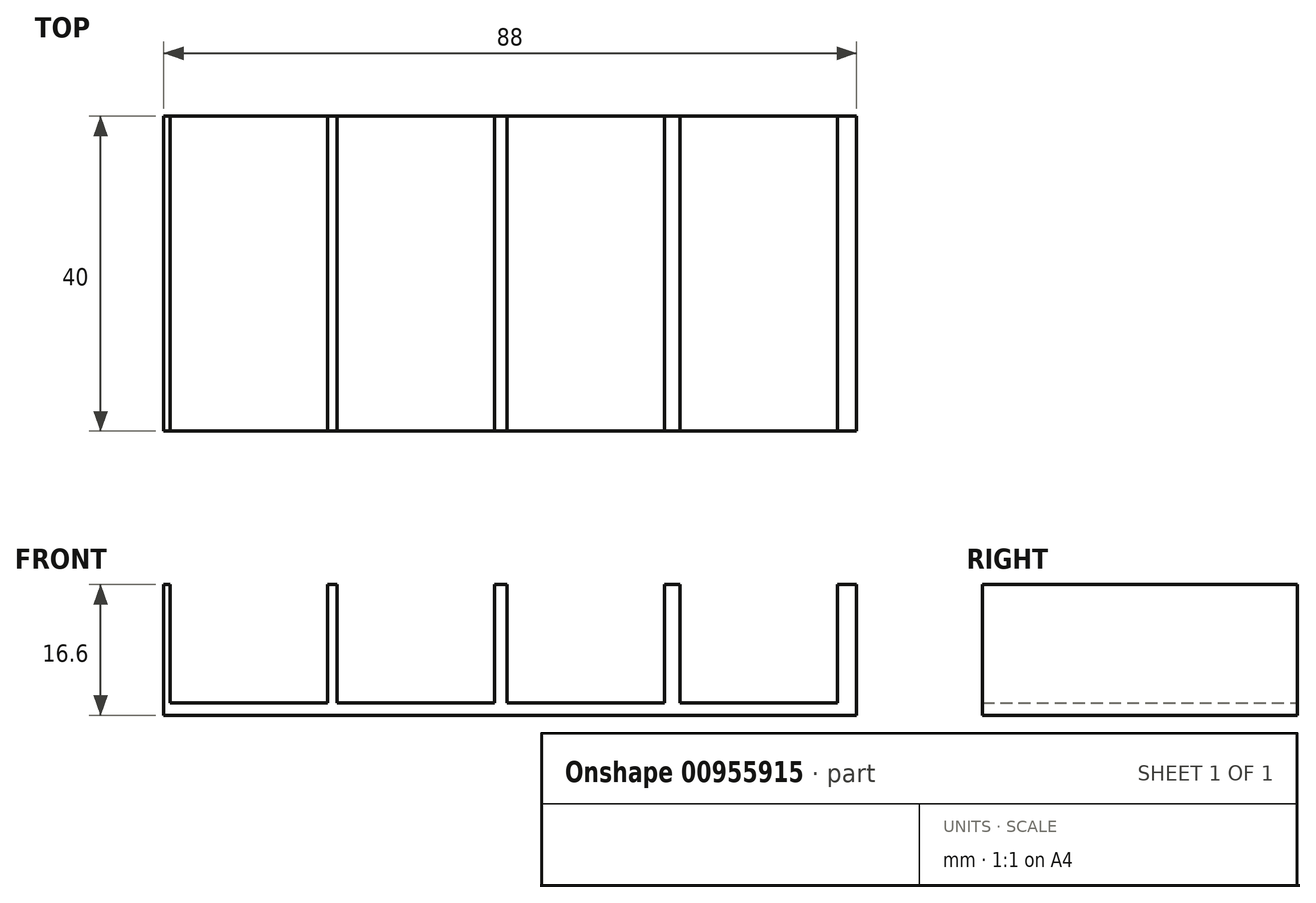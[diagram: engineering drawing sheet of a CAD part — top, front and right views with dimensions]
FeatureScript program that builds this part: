
annotation { "Feature Type Name" : "Feature", "Feature Type Description" : "" }
export const myFeature = defineFeature(function(context is Context, id is Id, definition is map)
    precondition{}
    {
        {
            var Q0;
            Q0=qCreatedBy(makeId("Top.planeOp"),FACE);
            var sketch = newSketch(context, id + "F0", { "sketchPlane" : qUnion([Q0])});
            skLineSegment(sketch, "E0.bottom", {"start": v(0, 0) * mm, "end": v(88, 0) * mm});
            skLineSegment(sketch, "E0.top", {"start": v(0, -40) * mm, "end": v(88, -40) * mm});
            skLineSegment(sketch, "E0.left", {"start": v(0, 0) * mm, "end": v(0, -40) * mm});
            skLineSegment(sketch, "E0.right", {"start": v(88, 0) * mm, "end": v(88, -40) * mm});
            skSolve(sketch);
        }
        {
            var Q0;
            Q0=makeQuery(id+"F0.imprint","IMPRINT",FACE,{"disambiguationData":[TD([[makeQuery(id+"F0.imprint","IMPRINT",EDGE,{"derivedFrom":sQuery(id+"F0.wireOp",EDGE,"E0.bottom")}),-1.0]])]});
            extrude(context, id + "F1", {"entities" : qUnion([Q0]), "depth" : 1.6 * mm, "offsetDistance" : 25 * mm});
        }
        {
            var Q0;
            Q0=makeQuery(id+"F1.opExtrude","CAP_FACE",FACE,{"disambiguationData":[OSD([sQuery(id+"F0.wireOp",EDGE,"E0.bottom"),sQuery(id+"F0.wireOp",EDGE,"E0.top"),sQuery(id+"F0.wireOp",EDGE,"E0.left"),sQuery(id+"F0.wireOp",EDGE,"E0.right")])],"isStart":false});
            var sketch = newSketch(context, id + "F2", { "sketchPlane" : qUnion([Q0])});
            skLineSegment(sketch, "E1.bottom", {"start": v(0, -40) * mm, "end": v(0.8, -40) * mm});
            skLineSegment(sketch, "E1.top", {"start": v(0, 0) * mm, "end": v(0.8, 0) * mm});
            skLineSegment(sketch, "E1.left", {"start": v(0, -40) * mm, "end": v(0, 0) * mm});
            skLineSegment(sketch, "E1.right", {"start": v(0.8, -40) * mm, "end": v(0.8, 0) * mm});
            skLineSegment(sketch, "E2.0", {"start": v(20.8, -40) * mm, "end": v(20.8, 0) * mm});
            skLineSegment(sketch, "E3.0", {"start": v(22, -40) * mm, "end": v(22, 0) * mm});
            skLineSegment(sketch, "E4.0", {"start": v(42, -40) * mm, "end": v(42, 0) * mm});
            skLineSegment(sketch, "E5.0", {"start": v(43.6, -40) * mm, "end": v(43.6, 0) * mm});
            skLineSegment(sketch, "E6.0", {"start": v(63.6, -40) * mm, "end": v(63.6, 0) * mm});
            skLineSegment(sketch, "E7.0", {"start": v(65.6, -40) * mm, "end": v(65.6, 0) * mm});
            skLineSegment(sketch, "E8.0", {"start": v(85.6, -40) * mm, "end": v(85.6, 0) * mm});
            skLineSegment(sketch, "E9.0", {"start": v(88, -40) * mm, "end": v(88, 0) * mm});
            skSolve(sketch);
        }
        {
            var Q0;
            Q0=makeQuery(id+"F2.imprint","IMPRINT",FACE,{"disambiguationData":[TD([[makeQuery(id+"F2.imprint","IMPRINT",EDGE,{"derivedFrom":sQuery(id+"F2.wireOp",EDGE,"E1.bottom")}),1.0]])]});
            var Q1;
            {var subQ0=sQuery(id+"F2.wireOp",EDGE,"E2.0");Q1=makeQuery(id+"F2.imprint","IMPRINT",FACE,{"disambiguationData":[TD([[makeQuery(id+"F2.imprint","IMPRINT",EDGE,{"derivedFrom":subQ0}),-1.0]])]});}
            var Q2;
            {var subQ0=sQuery(id+"F2.wireOp",EDGE,"E4.0");Q2=makeQuery(id+"F2.imprint","IMPRINT",FACE,{"disambiguationData":[TD([[makeQuery(id+"F2.imprint","IMPRINT",EDGE,{"derivedFrom":subQ0}),-1.0]])]});}
            var Q3;
            {var subQ0=sQuery(id+"F2.wireOp",EDGE,"E6.0");Q3=makeQuery(id+"F2.imprint","IMPRINT",FACE,{"disambiguationData":[TD([[makeQuery(id+"F2.imprint","IMPRINT",EDGE,{"derivedFrom":subQ0}),-1.0]])]});}
            var Q4;
            {var subQ0=sQuery(id+"F2.wireOp",EDGE,"E8.0");Q4=makeQuery(id+"F2.imprint","IMPRINT",FACE,{"disambiguationData":[TD([[makeQuery(id+"F2.imprint","IMPRINT",EDGE,{"derivedFrom":subQ0}),-1.0]])]});}
            extrude(context, id + "F3", {"entities" : qUnion([Q0, Q1, Q2, Q3, Q4]), "operationType" : NewBodyOperationType.ADD, "depth" : 15 * mm, "offsetDistance" : 25 * mm});
        }
    });
